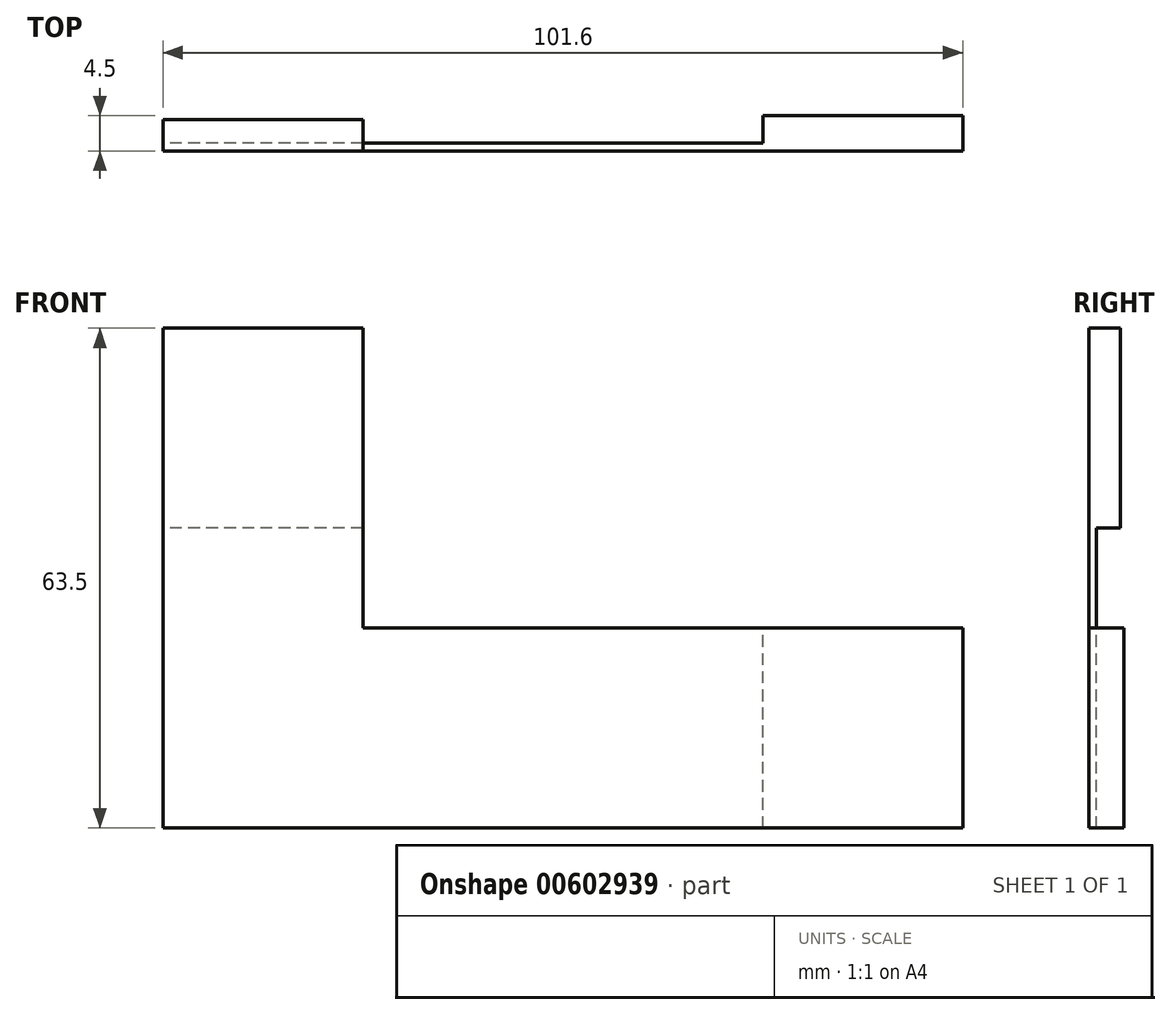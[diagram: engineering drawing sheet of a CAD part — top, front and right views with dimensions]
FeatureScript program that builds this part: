
annotation { "Feature Type Name" : "Feature", "Feature Type Description" : "" }
export const myFeature = defineFeature(function(context is Context, id is Id, definition is map)
    precondition{}
    {
        {
            assignVariable(context, id + "F0", {"name" : "X", "anyValue" : 1});
        }
        {
            assignVariable(context, id + "F1", {"name" : "C", "anyValue" : 3});
        }
        {
            assignVariable(context, id + "F2", {"name" : "D", "anyValue" : 3.5});
        }
        {
            var Q0;
            Q0=qCreatedBy(makeId("Front.planeOp"),FACE);
            var sketch = newSketch(context, id + "F3", { "sketchPlane" : qUnion([Q0])});
            skLineSegment(sketch, "E0.bottom", {"start": v(0, 0) * mm, "end": v(25.4, 0) * mm});
            skLineSegment(sketch, "E0.top", {"start": v(0, 63.5) * mm, "end": v(25.4, 63.5) * mm});
            skLineSegment(sketch, "E0.left", {"start": v(0, 0) * mm, "end": v(0, 63.5) * mm});
            skLineSegment(sketch, "E0.right", {"start": v(25.4, 25.4) * mm, "end": v(25.4, 63.5) * mm});
            skLineSegment(sketch, "E1.bottom", {"start": v(0, 0) * mm, "end": v(101.6, 0) * mm});
            skLineSegment(sketch, "E1.top", {"start": v(25.4, 25.4) * mm, "end": v(101.6, 25.4) * mm});
            skLineSegment(sketch, "E1.left", {"start": v(0, 0) * mm, "end": v(0, 25.4) * mm});
            skLineSegment(sketch, "E1.right", {"start": v(101.6, 0) * mm, "end": v(101.6, 25.4) * mm});
            skSolve(sketch);
        }
        {
            var Q0;
            Q0=makeQuery(id+"F3.imprint","IMPRINT",FACE,{"disambiguationData":[TD([[makeQuery(id+"F3.imprint","IMPRINT",EDGE,{"derivedFrom":sQuery(id+"F3.wireOp",EDGE,"E0.top")}),-1.0]])]});
            extrude(context, id + "F4", {"entities" : qUnion([Q0]), "oppositeDirection" : true, "depth" : (getVariable(context, 'X')) * mm, "offsetDistance" : 25.4 * mm});
        }
        {
            var Q0;
            Q0=makeQuery(id+"F4.opExtrude","CAP_FACE",FACE,{"disambiguationData":[OSD([sQuery(id+"F3.wireOp",EDGE,"E0.top"),sQuery(id+"F3.wireOp",EDGE,"E0.left"),sQuery(id+"F3.wireOp",EDGE,"E0.right"),sQuery(id+"F3.wireOp",EDGE,"E1.bottom"),sQuery(id+"F3.wireOp",EDGE,"E1.top"),sQuery(id+"F3.wireOp",EDGE,"E1.left"),sQuery(id+"F3.wireOp",EDGE,"E1.right")])],"isStart":false});
            var sketch = newSketch(context, id + "F5", { "sketchPlane" : qUnion([Q0])});
            skLineSegment(sketch, "E2.bottom", {"start": v(-25.4, 63.5) * mm, "end": v(0, 63.5) * mm});
            skLineSegment(sketch, "E2.top", {"start": v(-25.4, 38.1) * mm, "end": v(0, 38.1) * mm});
            skLineSegment(sketch, "E2.left", {"start": v(-25.4, 63.5) * mm, "end": v(-25.4, 38.1) * mm});
            skLineSegment(sketch, "E2.right", {"start": v(0, 63.5) * mm, "end": v(0, 38.1) * mm});
            skSolve(sketch);
        }
        {
            var Q0;
            Q0=makeQuery(id+"F5.imprint","IMPRINT",FACE,{"disambiguationData":[TD([[makeQuery(id+"F5.imprint","IMPRINT",EDGE,{"derivedFrom":sQuery(id+"F5.wireOp",EDGE,"E2.bottom")}),1.0]])]});
            extrude(context, id + "F6", {"entities" : qUnion([Q0]), "operationType" : NewBodyOperationType.ADD, "depth" : (getVariable(context, 'C')) * mm, "offsetDistance" : 25.4 * mm});
        }
        {
            var Q0;
            Q0=makeQuery(id+"F4.opExtrude","CAP_FACE",FACE,{"disambiguationData":[OSD([sQuery(id+"F3.wireOp",EDGE,"E0.top"),sQuery(id+"F3.wireOp",EDGE,"E0.left"),sQuery(id+"F3.wireOp",EDGE,"E0.right"),sQuery(id+"F3.wireOp",EDGE,"E1.bottom"),sQuery(id+"F3.wireOp",EDGE,"E1.top"),sQuery(id+"F3.wireOp",EDGE,"E1.left"),sQuery(id+"F3.wireOp",EDGE,"E1.right")])],"isStart":false});
            var sketch = newSketch(context, id + "F7", { "sketchPlane" : qUnion([Q0])});
            skLineSegment(sketch, "E3.bottom", {"start": v(-76.2, 0) * mm, "end": v(-101.6, 0) * mm});
            skLineSegment(sketch, "E3.top", {"start": v(-76.2, 25.4) * mm, "end": v(-101.6, 25.4) * mm});
            skLineSegment(sketch, "E3.left", {"start": v(-76.2, 0) * mm, "end": v(-76.2, 25.4) * mm});
            skLineSegment(sketch, "E3.right", {"start": v(-101.6, 0) * mm, "end": v(-101.6, 25.4) * mm});
            skSolve(sketch);
        }
        {
            var Q0;
            Q0=makeQuery(id+"F7.imprint","IMPRINT",FACE,{"disambiguationData":[TD([[makeQuery(id+"F7.imprint","IMPRINT",EDGE,{"derivedFrom":sQuery(id+"F7.wireOp",EDGE,"E3.bottom")}),-1.0]])]});
            extrude(context, id + "F8", {"entities" : qUnion([Q0]), "operationType" : NewBodyOperationType.ADD, "depth" : (getVariable(context, 'D')) * mm, "offsetDistance" : 25.4 * mm});
        }
    });
